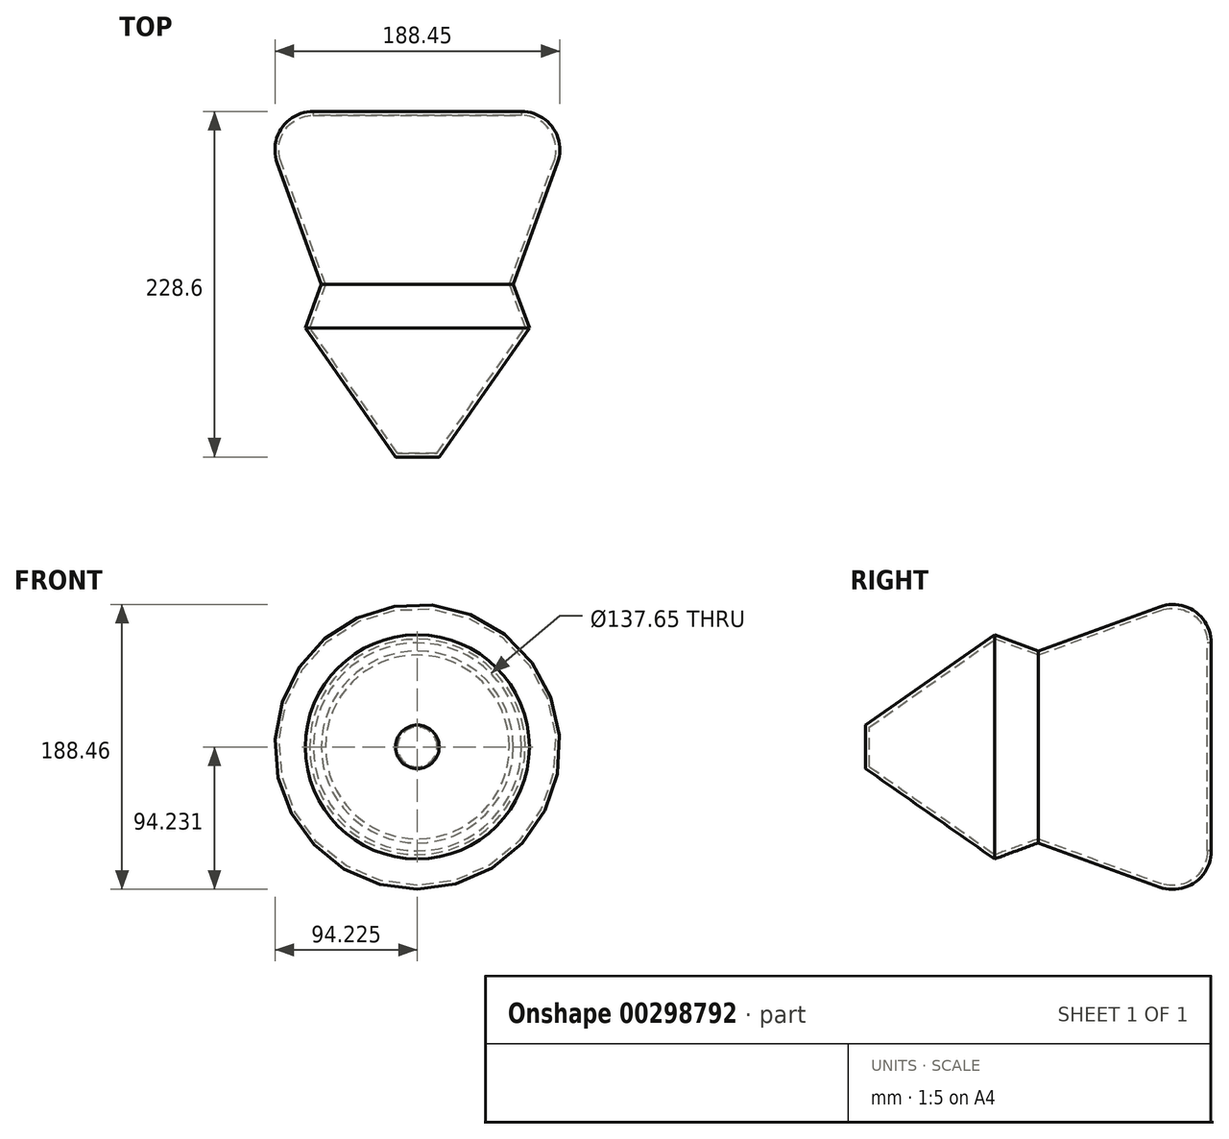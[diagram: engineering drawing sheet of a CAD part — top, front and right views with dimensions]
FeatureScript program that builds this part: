
annotation { "Feature Type Name" : "Feature", "Feature Type Description" : "" }
export const myFeature = defineFeature(function(context is Context, id is Id, definition is map)
    precondition{}
    {
        {
            var Q0;
            Q0=qCreatedBy(makeId("Front.planeOp"),FACE);
            var sketch = newSketch(context, id + "F0", { "sketchPlane" : qUnion([Q0])});
            skCircle(sketch, "E0", {"center": v(-2.93, 3.7) * mm, "radius": 63.5 * mm});
            skSolve(sketch);
        }
        {
            var Q0;
            Q0 = qSketchRegion(id + "F0", true);
            extrude(context, id + "F1", {"entities" : qUnion([Q0]), "endBound" : BoundingType.SYMMETRIC, "depth" : 228.6 * mm, "hasDraft" : true, "draftAngle" : 20 * degree});
        }
        {
            var Q0;
            Q0=makeQuery(id+"F1.opExtrude","CAP_EDGE",EDGE,{"disambiguationData":[OSD([sQuery(id+"F0.wireOp",EDGE,"E0")])],"isStart":true});
            fillet(context, id + "F2", {"entities" : qUnion([Q0]), "radius" : 25.4 * mm, "tangentPropagation" : true, "allowEdgeOverflow" : false});
        }
        {
            var Q0;
            Q0=makeQuery(id+"F1.opExtrude","CAP_EDGE",EDGE,{"disambiguationData":[OSD([sQuery(id+"F0.wireOp",EDGE,"E0")])],"isStart":false});
            chamfer(context, id + "F3", {"entities" : qUnion([Q0]), "width" : 63.5 * mm, "tangentPropagation" : true});
        }
        {
            var Q0;
            Q0=makeQuery(id+"F1.opExtrude","CAP_FACE",FACE,{"disambiguationData":[OSD([sQuery(id+"F0.wireOp",EDGE,"E0")])],"isStart":true});
            shell(context, id + "F4", {"entities" : qUnion([Q0]), "thickness" : 2.54 * mm});
        }
    });
